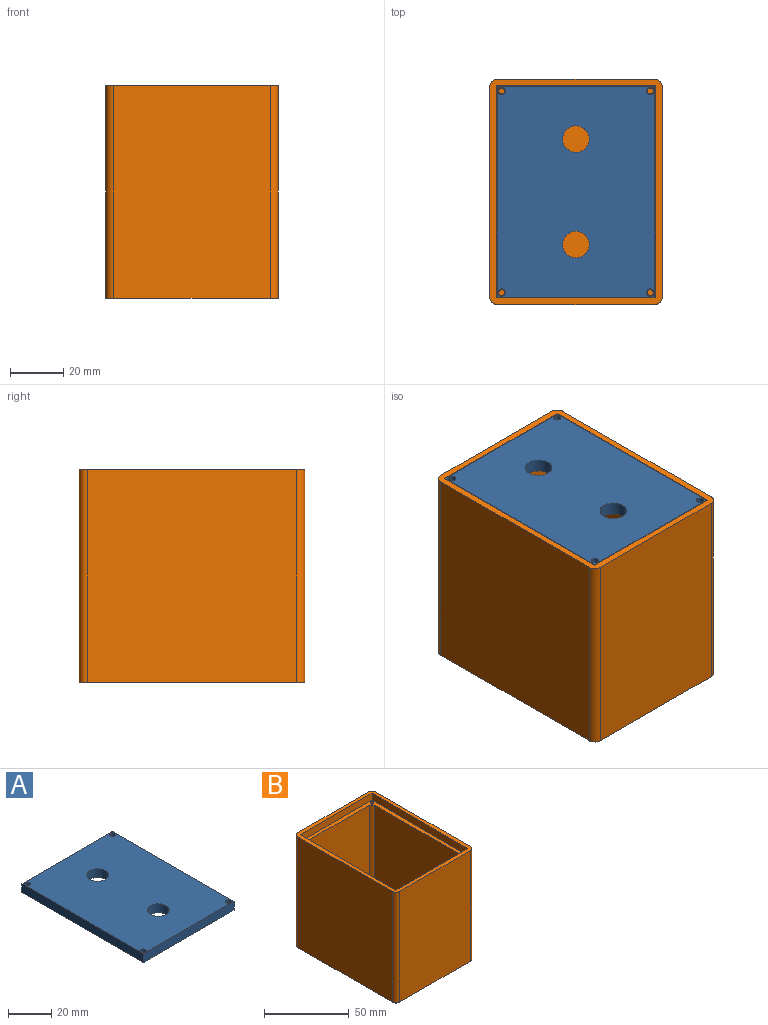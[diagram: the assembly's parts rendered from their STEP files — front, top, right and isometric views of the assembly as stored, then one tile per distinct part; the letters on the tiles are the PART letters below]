
ASSEMBLY  parts=2 mates=1
PART A: 12 faces, bbox 59.5x79.5x5 mm
  f0: plane 79.5x5mm, normal (1,0,0), area 397.5mm2, adj f1,f3,f4,f5
  f1: plane 59.5x5mm, normal (0,1,0), area 297.5mm2, adj f0,f2,f4,f5
  f2: plane 79.5x5mm, normal (-1,0,0), area 397.5mm2, adj f1,f3,f4,f5
  f3: plane 59.5x5mm, normal (0,-1,0), area 297.5mm2, adj f0,f2,f4,f5
  f4: plane 79.5x59.5mm, normal (0,0,1), area 4548.5mm2, adj f0,f1,f2,f3,f6,f7,f8,f9
  f5: plane 79.5x59.5mm, normal (0,0,-1), area 4548.5mm2, adj f0,f1,f2,f3,f6,f7,f8,f9
  f6: cylinder r=1.4mm len=5mm, axis (0,0,1), area 44mm2, adj f4,f5
  f7: cylinder r=1.4mm len=5mm, axis (0,0,1), area 44mm2, adj f4,f5
  f8: cylinder r=1.4mm len=5mm, axis (0,0,1), area 44mm2, adj f4,f5
  f9: cylinder r=1.4mm len=5mm, axis (0,0,1), area 44mm2, adj f4,f5
  f10: cylinder r=5mm len=10mm, axis (0,0,1), area 157.1mm2, adj f4,f5
  f11: cylinder r=5mm len=10mm, axis (0,0,1), area 157.1mm2, adj f4,f5
PART B: 36 faces, bbox 65x85x80 mm
  f0: plane 85x65mm, normal (0,0,1), area 717.3mm2, adj f1,f2,f3,f4,f6,f7,f8,f9
  f1: plane 80x79mm, normal (1,0,0), area 6320mm2, adj f0,f5,f32,f35
  f2: plane 80x59mm, normal (0,1,0), area 4720mm2, adj f0,f5,f32,f33
  f3: plane 80x79mm, normal (-1,0,0), area 6320mm2, adj f0,f5,f33,f34
  f4: plane 80x59mm, normal (0,-1,0), area 4720mm2, adj f0,f5,f34,f35
  f5: plane 85x65mm, normal (0,0,-1), area 5501.2mm2, adj f1,f2,f3,f4,f28,f29,f30,f31
  f6: plane 60x5mm, normal (0,-1,0), area 300mm2, adj f0,f7,f9,f10
  f7: plane 80x5mm, normal (1,0,0), area 400mm2, adj f0,f6,f8,f10
  f8: plane 60x5mm, normal (0,1,0), area 300mm2, adj f0,f7,f9,f10
  f9: plane 80x5mm, normal (-1,0,0), area 400mm2, adj f0,f6,f8,f10
  f10: plane 80x60mm, normal (0,0,1), area 670.1mm2, adj f6,f7,f8,f9,f12,f13,f14,f15
  f11: plane 75x55mm, normal (0,0,1), area 4097.8mm2, adj f12,f13,f14,f15,f16,f17,f18,f19
  f12: cylinder r=4.42mm len=70mm, axis (0,0,1), area 214.8mm2, adj f10,f11,f13,f19
  f13: plane 70x50.75mm, normal (0,1,0), area 3552.2mm2, adj f10,f11,f12,f14
  f14: cylinder r=4.42mm len=70mm, axis (0,0,1), area 214.8mm2, adj f10,f11,f13,f15
  f15: plane 70.75x70mm, normal (1,0,0), area 4952.2mm2, adj f10,f11,f14,f16
  f16: cylinder r=4.42mm len=70mm, axis (0,0,1), area 214.8mm2, adj f10,f11,f15,f17
  f17: plane 70x50.75mm, normal (0,-1,0), area 3552.2mm2, adj f10,f11,f16,f18
  f18: cylinder r=4.42mm len=70mm, axis (0,0,1), area 214.8mm2, adj f10,f11,f17,f19
  f19: plane 70.75x70mm, normal (-1,0,0), area 4952.2mm2, adj f10,f11,f12,f18
  f20: cylinder r=1.13mm len=10mm, axis (0,0,1), area 71mm2, adj f10,f21
  f21: plane 2.26x2.26mm, normal (0,0,1), area 4mm2, adj f20
  f22: cylinder r=1.13mm len=10mm, axis (0,0,1), area 71mm2, adj f10,f23
  f23: plane 2.26x2.26mm, normal (0,0,1), area 4mm2, adj f22
  f24: cylinder r=1.13mm len=10mm, axis (0,0,1), area 71mm2, adj f10,f25
  f25: plane 2.26x2.26mm, normal (0,0,1), area 4mm2, adj f24
  f26: cylinder r=1.13mm len=10mm, axis (0,0,1), area 71mm2, adj f10,f27
  f27: plane 2.26x2.26mm, normal (0,0,1), area 4mm2, adj f26
  f28: cylinder r=1.13mm len=5mm, axis (0,0,-1), area 35.5mm2, adj f5,f11
  f29: cylinder r=1.13mm len=5mm, axis (0,0,-1), area 35.5mm2, adj f5,f11
  f30: cylinder r=1.13mm len=5mm, axis (0,0,-1), area 35.5mm2, adj f5,f11
  f31: cylinder r=1.13mm len=5mm, axis (0,0,-1), area 35.5mm2, adj f5,f11
  f32: cylinder r=3mm len=80mm, axis (0,0,1), area 377mm2, adj f0,f1,f2,f5
  f33: cylinder r=3mm len=80mm, axis (0,0,-1), area 377mm2, adj f0,f2,f3,f5
  f34: cylinder r=3mm len=80mm, axis (0,0,1), area 377mm2, adj f0,f3,f4,f5
  f35: cylinder r=3mm len=80mm, axis (0,0,-1), area 377mm2, adj f0,f1,f4,f5
PLACE A t=(-24.25,61.95,-2.5)mm
PLACE B t=(-24.25,61.95,-77.5)mm
MATE fastened B.f24 <-> A.f7  axis (0,0,1) through (-52.25,23.95,-2.5)mm
